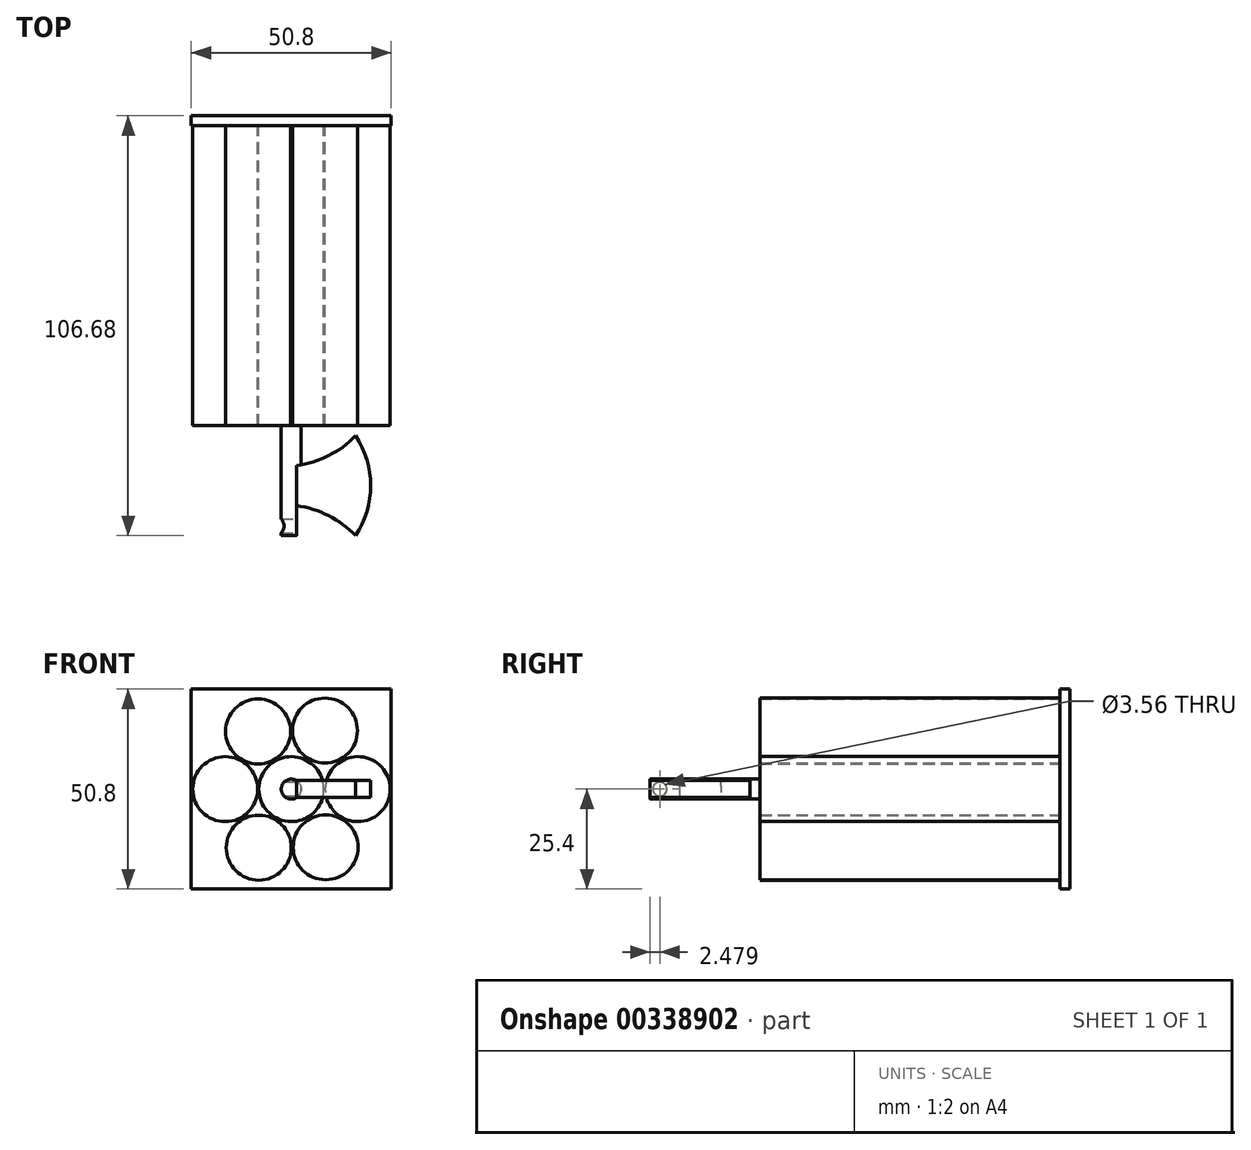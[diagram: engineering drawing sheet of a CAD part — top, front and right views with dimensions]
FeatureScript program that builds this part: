
annotation { "Feature Type Name" : "Feature", "Feature Type Description" : "" }
export const myFeature = defineFeature(function(context is Context, id is Id, definition is map)
    precondition{}
    {
        {
            var Q0;
            Q0=qCreatedBy(makeId("Front.planeOp"),FACE);
            var sketch = newSketch(context, id + "F0", { "sketchPlane" : qUnion([Q0])});
            skLineSegment(sketch, "E0.bottom", {"start": v(25.4, -25.4) * mm, "end": v(-25.4, -25.4) * mm});
            skLineSegment(sketch, "E0.top", {"start": v(25.4, 25.4) * mm, "end": v(-25.4, 25.4) * mm});
            skLineSegment(sketch, "E0.left", {"start": v(25.4, -25.4) * mm, "end": v(25.4, 25.4) * mm});
            skLineSegment(sketch, "E0.right", {"start": v(-25.4, -25.4) * mm, "end": v(-25.4, 25.4) * mm});
            skPoint(sketch, "E0.middle", {"position": v(0, 0) * mm});
            skSolve(sketch);
        }
        {
            var Q0;
            Q0 = qSketchRegion(id + "F0", true);
            extrude(context, id + "F1", {"entities" : qUnion([Q0]), "depth" : 2.54 * mm});
        }
        {
            var Q0;
            Q0=makeQuery(id+"F1.opExtrude","CAP_FACE",FACE,{"disambiguationData":[OSD([sQuery(id+"F0.wireOp",EDGE,"E0.bottom"),sQuery(id+"F0.wireOp",EDGE,"E0.top"),sQuery(id+"F0.wireOp",EDGE,"E0.left"),sQuery(id+"F0.wireOp",EDGE,"E0.right")])],"isStart":false});
            var sketch = newSketch(context, id + "F2", { "sketchPlane" : qUnion([Q0])});
            skCircle(sketch, "E1", {"center": v(0, 0) * mm, "radius": 8.26 * mm});
            skPoint(sketch, "E2.first.point", {"position": v(-8.26, 0) * mm});
            skPoint(sketch, "E2.second.point", {"position": v(-20.08, 7.44) * mm});
            skPoint(sketch, "E2.third.point", {"position": v(-20.83, -7.04) * mm});
            skPoint(sketch, "E3.first.point", {"position": v(-12.24, 7.07) * mm});
            skPoint(sketch, "E3.second.point", {"position": v(-2.67, 7.81) * mm});
            skPoint(sketch, "E3.third.point", {"position": v(-6.35, 22.23) * mm});
            skPoint(sketch, "E4.first.point", {"position": v(0.28, 14.09) * mm});
            skPoint(sketch, "E4.second.point", {"position": v(3.56, 7.45) * mm});
            skPoint(sketch, "E4.third.point", {"position": v(15.79, 10.1) * mm});
            skPoint(sketch, "E5.first.point", {"position": v(8.25, -0.13) * mm});
            skPoint(sketch, "E5.second.point", {"position": v(24.2, -3.24) * mm});
            skPoint(sketch, "E5.third.point", {"position": v(11.58, 6.37) * mm});
            skPoint(sketch, "E6.first.point", {"position": v(-4.18, -7.12) * mm});
            skPoint(sketch, "E6.second.point", {"position": v(-8.91, -22.47) * mm});
            skPoint(sketch, "E6.third.point", {"position": v(-13.26, -7.59) * mm});
            skPoint(sketch, "E7.first.point", {"position": v(-0.18, -15.3) * mm});
            skPoint(sketch, "E7.second.point", {"position": v(12.3, -7.36) * mm});
            skPoint(sketch, "E7.third.point", {"position": v(3.9, -7.28) * mm});
            skSolve(sketch);
        }
        {
            var Q0;
            Q0=makeQuery(id+"F2.imprint","IMPRINT",FACE,{"disambiguationData":[TD([[makeQuery(id+"F2.imprint","IMPRINT",EDGE,{"derivedFrom":sQuery(id+"F2.wireOp",EDGE,"E1")}),1.0]])]});
            extrude(context, id + "F3", {"entities" : qUnion([Q0]), "operationType" : NewBodyOperationType.ADD, "depth" : 76.2 * mm});
        }
        {
            var Q0;
            Q0=makeQuery(id+"F1.opExtrude","CAP_FACE",FACE,{"disambiguationData":[OSD([sQuery(id+"F0.wireOp",EDGE,"E0.bottom"),sQuery(id+"F0.wireOp",EDGE,"E0.top"),sQuery(id+"F0.wireOp",EDGE,"E0.left"),sQuery(id+"F0.wireOp",EDGE,"E0.right")])],"isStart":false});
            var sketch = newSketch(context, id + "F4", { "sketchPlane" : qUnion([Q0])});
            skCircle(sketch, "E8", {"center": v(0, 0) * mm, "radius": 8.26 * mm});
            skPoint(sketch, "E9.first.point", {"position": v(-8.26, 0) * mm});
            skPoint(sketch, "E9.second.point", {"position": v(-23.27, 4.74) * mm});
            skPoint(sketch, "E9.third.point", {"position": v(-23.6, -4.24) * mm});
            skCircle(sketch, "E10", {"center": v(-16.78, 0) * mm, "radius": 8.26 * mm});
            skSolve(sketch);
        }
        {
            var Q0;
            Q0=makeQuery(id+"F1.opExtrude","CAP_FACE",FACE,{"disambiguationData":[OSD([sQuery(id+"F0.wireOp",EDGE,"E0.bottom"),sQuery(id+"F0.wireOp",EDGE,"E0.top"),sQuery(id+"F0.wireOp",EDGE,"E0.left"),sQuery(id+"F0.wireOp",EDGE,"E0.right")])],"isStart":false});
            var sketch = newSketch(context, id + "F5", { "sketchPlane" : qUnion([Q0])});
            skCircle(sketch, "E11", {"center": v(0, 0) * mm, "radius": 8.26 * mm});
            skPoint(sketch, "E12.first.point", {"position": v(8.26, 0) * mm});
            skPoint(sketch, "E12.second.point", {"position": v(20.98, 5.72) * mm});
            skPoint(sketch, "E12.third.point", {"position": v(22.26, -7) * mm});
            skCircle(sketch, "E13", {"center": v(16.88, 0) * mm, "radius": 8.26 * mm});
            skPoint(sketch, "E14.first.point", {"position": v(22.55, -0.48) * mm});
            skSolve(sketch);
        }
        {
            var Q0;
            Q0 = qSketchRegion(id + "F5", true);
            extrude(context, id + "F6", {"entities" : qUnion([Q0]), "operationType" : NewBodyOperationType.ADD, "depth" : 76.2 * mm});
        }
        {
            var Q0;
            Q0=makeQuery(id+"F4.imprint","IMPRINT",FACE,{"disambiguationData":[TD([[makeQuery(id+"F4.imprint","IMPRINT",EDGE,{"derivedFrom":sQuery(id+"F4.wireOp",EDGE,"E10")}),1.0]])]});
            extrude(context, id + "F7", {"entities" : qUnion([Q0]), "operationType" : NewBodyOperationType.ADD, "depth" : 76.2 * mm});
        }
        {
            var Q0;
            Q0=makeQuery(id+"F1.opExtrude","CAP_FACE",FACE,{"disambiguationData":[OSD([sQuery(id+"F0.wireOp",EDGE,"E0.bottom"),sQuery(id+"F0.wireOp",EDGE,"E0.top"),sQuery(id+"F0.wireOp",EDGE,"E0.left"),sQuery(id+"F0.wireOp",EDGE,"E0.right")])],"isStart":false});
            var sketch = newSketch(context, id + "F8", { "sketchPlane" : qUnion([Q0])});
            skCircle(sketch, "E15", {"center": v(-8.44, 14.68) * mm, "radius": 8.26 * mm});
            skSolve(sketch);
        }
        {
            var Q0;
            Q0=makeQuery(id+"F8.imprint","IMPRINT",FACE,{"disambiguationData":[TD([[makeQuery(id+"F8.imprint","IMPRINT",EDGE,{"derivedFrom":sQuery(id+"F8.wireOp",EDGE,"E15")}),1.0]])]});
            extrude(context, id + "F9", {"entities" : qUnion([Q0]), "operationType" : NewBodyOperationType.ADD, "depth" : 76.2 * mm});
        }
        {
            var Q0;
            Q0=makeQuery(id+"F1.opExtrude","CAP_FACE",FACE,{"disambiguationData":[OSD([sQuery(id+"F0.wireOp",EDGE,"E0.bottom"),sQuery(id+"F0.wireOp",EDGE,"E0.top"),sQuery(id+"F0.wireOp",EDGE,"E0.left"),sQuery(id+"F0.wireOp",EDGE,"E0.right")])],"isStart":false});
            var sketch = newSketch(context, id + "F10", { "sketchPlane" : qUnion([Q0])});
            skCircle(sketch, "E16", {"center": v(8.54, 14.87) * mm, "radius": 8.26 * mm});
            skSolve(sketch);
        }
        {
            var Q0;
            Q0=makeQuery(id+"F10.imprint","IMPRINT",FACE,{"disambiguationData":[TD([[makeQuery(id+"F10.imprint","IMPRINT",EDGE,{"derivedFrom":sQuery(id+"F10.wireOp",EDGE,"E16")}),1.0]])]});
            extrude(context, id + "F11", {"entities" : qUnion([Q0]), "operationType" : NewBodyOperationType.ADD, "depth" : 76.2 * mm});
        }
        {
            var Q0;
            Q0=makeQuery(id+"F1.opExtrude","CAP_FACE",FACE,{"disambiguationData":[OSD([sQuery(id+"F0.wireOp",EDGE,"E0.bottom"),sQuery(id+"F0.wireOp",EDGE,"E0.top"),sQuery(id+"F0.wireOp",EDGE,"E0.left"),sQuery(id+"F0.wireOp",EDGE,"E0.right")])],"isStart":false});
            var sketch = newSketch(context, id + "F12", { "sketchPlane" : qUnion([Q0])});
            skCircle(sketch, "E17", {"center": v(-8.25, -14.87) * mm, "radius": 8.26 * mm});
            skSolve(sketch);
        }
        {
            var Q0;
            Q0 = qSketchRegion(id + "F12", true);
            extrude(context, id + "F13", {"entities" : qUnion([Q0]), "operationType" : NewBodyOperationType.ADD, "depth" : 76.2 * mm});
        }
        {
            var Q0;
            Q0=makeQuery(id+"F1.opExtrude","CAP_FACE",FACE,{"disambiguationData":[OSD([sQuery(id+"F0.wireOp",EDGE,"E0.bottom"),sQuery(id+"F0.wireOp",EDGE,"E0.top"),sQuery(id+"F0.wireOp",EDGE,"E0.left"),sQuery(id+"F0.wireOp",EDGE,"E0.right")])],"isStart":false});
            var sketch = newSketch(context, id + "F14", { "sketchPlane" : qUnion([Q0])});
            skCircle(sketch, "E18", {"center": v(8.73, -14.77) * mm, "radius": 8.26 * mm});
            skSolve(sketch);
        }
        {
            var Q0;
            Q0=makeQuery(id+"F14.imprint","IMPRINT",FACE,{"disambiguationData":[TD([[makeQuery(id+"F14.imprint","IMPRINT",EDGE,{"derivedFrom":sQuery(id+"F14.wireOp",EDGE,"E18")}),1.0]])]});
            extrude(context, id + "F15", {"entities" : qUnion([Q0]), "operationType" : NewBodyOperationType.ADD, "depth" : 76.2 * mm});
        }
        {
            var Q0;
            Q0=makeQuery(id+"F3.opExtrude","CAP_FACE",FACE,{"disambiguationData":[OSD([sQuery(id+"F2.wireOp",EDGE,"E1")])],"isStart":false});
            var sketch = newSketch(context, id + "F16", { "sketchPlane" : qUnion([Q0])});
            skCircle(sketch, "E19", {"center": v(0, 0) * mm, "radius": 2.54 * mm});
            skSolve(sketch);
        }
        {
            var Q0;
            Q0 = qSketchRegion(id + "F16", true);
            extrude(context, id + "F17", {"entities" : qUnion([Q0]), "operationType" : NewBodyOperationType.ADD, "depth" : 27.94 * mm});
        }
        {
            var Q0;
            Q0=makeQuery(id+"F17.opExtrude","CAP_FACE",FACE,{"disambiguationData":[OSD([sQuery(id+"F16.wireOp",EDGE,"E19")])],"isStart":false});
            var sketch = newSketch(context, id + "F18", { "sketchPlane" : qUnion([Q0])});
            skLineSegment(sketch, "E20", {"start": v(1.34, 2.17) * mm, "end": v(1.34, -2.15) * mm});
            skArc(sketch, "E21", {"start": v(1.34, -2.15) * mm, "mid": v(2.54, 0) * mm, "end": v(1.34, 2.17) * mm});
            skSolve(sketch);
        }
        {
            var Q0;
            Q0 = qSketchRegion(id + "F18", true);
            extrude(context, id + "F19", {"entities" : qUnion([Q0]), "operationType" : NewBodyOperationType.REMOVE, "oppositeDirection" : true, "depth" : 25.4 * mm});
        }
        {
            var Q0;
            Q0=makeQuery(id+"F19.boolean.opBoolean","COPY",FACE,{"derivedFrom":makeQuery(id+"F19.opExtrude","SWEPT_FACE",FACE,{"disambiguationData":[OSD([sQuery(id+"F18.wireOp",EDGE,"E20")])]})});
            var sketch = newSketch(context, id + "F20", { "sketchPlane" : qUnion([Q0])});
            skLineSegment(sketch, "E22.bottom", {"start": v(-106.68, -2.16) * mm, "end": v(-81.28, -2.16) * mm});
            skLineSegment(sketch, "E22.top", {"start": v(-106.68, 2.17) * mm, "end": v(-81.28, 2.17) * mm});
            skLineSegment(sketch, "E22.left", {"start": v(-106.68, -2.16) * mm, "end": v(-106.68, 2.17) * mm});
            skLineSegment(sketch, "E22.right", {"start": v(-81.28, -2.16) * mm, "end": v(-81.28, 2.17) * mm});
            skSolve(sketch);
        }
        {
            var Q0;
            Q0=makeQuery(id+"F20.imprint","IMPRINT",FACE,{"disambiguationData":[TD([[makeQuery(id+"F20.imprint","IMPRINT",EDGE,{"derivedFrom":sQuery(id+"F20.wireOp",EDGE,"E22.bottom")}),1.0]])]});
            var Q1;
            Q1=makeQuery(id+"F20.imprint","IMPRINT",FACE,{"disambiguationData":[TD([[makeQuery(id+"F20.imprint","IMPRINT",EDGE,{"derivedFrom":sQuery(id+"F20.wireOp",EDGE,"E22.top")}),1.0]])]});
            extrude(context, id + "F21", {"entities" : qUnion([Q0, Q1]), "operationType" : NewBodyOperationType.ADD, "depth" : 25.4 * mm});
        }
        {
            var Q0;
            Q0=makeQuery(id+"F21.opExtrude","SWEPT_FACE",FACE,{"disambiguationData":[OSD([sQuery(id+"F20.wireOp",EDGE,"E22.bottom")])]});
            var sketch = newSketch(context, id + "F22", { "sketchPlane" : qUnion([Q0])});
            skArc(sketch, "E23", {"start": v(1.34, 99.06) * mm, "mid": v(9.47, 101.6) * mm, "end": v(16.3, 106.68) * mm});
            skArc(sketch, "E24", {"start": v(16.3, 81.28) * mm, "mid": v(9.47, 86.36) * mm, "end": v(1.34, 88.9) * mm});
            skArc(sketch, "E25", {"start": v(16.3, 81.28) * mm, "mid": v(20.17, 93.98) * mm, "end": v(16.3, 106.68) * mm});
            skLineSegment(sketch, "E26", {"start": v(16.3, 106.68) * mm, "end": v(16.3, 81.28) * mm});
            skSolve(sketch);
        }
        {
            var Q0;
            {var subQ0=sQuery(id+"F22.wireOp",EDGE,"E23");Q0=makeQuery(id+"F22.imprint","IMPRINT",FACE,{"disambiguationData":[TD([[makeQuery(id+"F22.imprint","IMPRINT",EDGE,{"derivedFrom":subQ0}),1.0]])]});}
            var Q1;
            {var subQ0=sQuery(id+"F22.wireOp",EDGE,"E25");Q1=makeQuery(id+"F22.imprint","IMPRINT",FACE,{"disambiguationData":[TD([[makeQuery(id+"F22.imprint","IMPRINT",EDGE,{"derivedFrom":subQ0}),-1.0]])]});}
            var Q2;
            {var subQ0=sQuery(id+"F22.wireOp",EDGE,"E24");Q2=makeQuery(id+"F22.imprint","IMPRINT",FACE,{"disambiguationData":[TD([[makeQuery(id+"F22.imprint","IMPRINT",EDGE,{"derivedFrom":subQ0}),1.0]])]});}
            extrude(context, id + "F23", {"entities" : qUnion([Q0, Q1, Q2]), "operationType" : NewBodyOperationType.REMOVE, "oppositeDirection" : true, "depth" : 25.4 * mm});
        }
        {
            var Q0;
            {var subQ0=sQuery(id+"F20.wireOp",EDGE,"E22.bottom");var subQ3=sQuery(id+"F20.wireOp",EDGE,"E22.right");var subQ4=makeQuery(id+"F21.opExtrude","SWEPT_EDGE",EDGE,{"disambiguationData":[OSD([subQ0,subQ3])]});Q0=makeQuery(id+"F23.boolean.opBoolean","COPY",FACE,{"derivedFrom":makeQuery(id+"F23.opExtrude","SWEPT_FACE",FACE,{"disambiguationData":[OSD([subQ0,subQ3]),TDD([makeQuery(id+"F22.imprint","IMPRINT",EDGE,{"disambiguationData":[TD([[makeQuery(id+"F22.imprint","INTERSECT",VERTEX,{"derivedFrom":[subQ4,sQuery(id+"F22.wireOp",EDGE,"E24"),sQuery(id+"F22.wireOp",EDGE,"E25"),sQuery(id+"F22.wireOp",EDGE,"E26")]}),1.0]])],"derivedFrom":subQ4})])]})});}
            var sketch = newSketch(context, id + "F24", { "sketchPlane" : qUnion([Q0])});
            skArc(sketch, "E27", {"start": v(1.34, -2.15) * mm, "mid": v(2.54, 0) * mm, "end": v(1.34, 2.16) * mm});
            skSolve(sketch);
        }
        {
            var Q0;
            Q0=makeQuery(id+"F24.imprint","IMPRINT",FACE,{"disambiguationData":[TD([[makeQuery(id+"F24.imprint","IMPRINT",EDGE,{"derivedFrom":sQuery(id+"F24.wireOp",EDGE,"E27")}),1.0]])]});
            extrude(context, id + "F25", {"entities" : qUnion([Q0]), "operationType" : NewBodyOperationType.ADD, "depth" : 17.78 * mm});
        }
        {
            var Q0;
            {var subQ0=sQuery(id+"F20.wireOp",EDGE,"E22.bottom");var subQ1=sQuery(id+"F18.wireOp",EDGE,"E21");var subQ2=sQuery(id+"F18.wireOp",EDGE,"E20");var subQ3=makeQuery(id+"F21.boolean.opBoolean","MERGE",EDGE,{"derivedFrom":[makeQuery(id+"F19.boolean.opBoolean","COPY",EDGE,{"derivedFrom":makeQuery(id+"F19.opExtrude","SWEPT_EDGE",EDGE,{"disambiguationData":[OSD([subQ2,subQ1]),TDD([makeQuery(id+"F18.imprint","INTERSECT",VERTEX,{"disambiguationData":[OD(1.0)],"derivedFrom":[subQ2,subQ1]})])]})}),makeQuery(id+"F21.opExtrude","CAP_EDGE",EDGE,{"disambiguationData":[OSD([subQ0])],"isStart":true})]});Q0=makeQuery(id+"F23.boolean.opBoolean","COPY",FACE,{"derivedFrom":makeQuery(id+"F23.opExtrude","SWEPT_FACE",FACE,{"disambiguationData":[OSD([subQ2,subQ1,subQ0]),TDD([makeQuery(id+"F22.imprint","IMPRINT",EDGE,{"disambiguationData":[TD([[makeQuery(id+"F22.imprint","INTERSECT",VERTEX,{"derivedFrom":[subQ3,sQuery(id+"F22.wireOp",EDGE,"E23")]}),1.0]])],"derivedFrom":subQ3})])]})});}
            var sketch = newSketch(context, id + "F26", { "sketchPlane" : qUnion([Q0])});
            skCircle(sketch, "E28", {"center": v(-104.2, 0) * mm, "radius": 1.78 * mm});
            skSolve(sketch);
        }
        {
            var Q0;
            Q0 = qSketchRegion(id + "F26", true);
            extrude(context, id + "F27", {"entities" : qUnion([Q0]), "operationType" : NewBodyOperationType.REMOVE, "oppositeDirection" : true, "depth" : 25.4 * mm});
        }
    });
